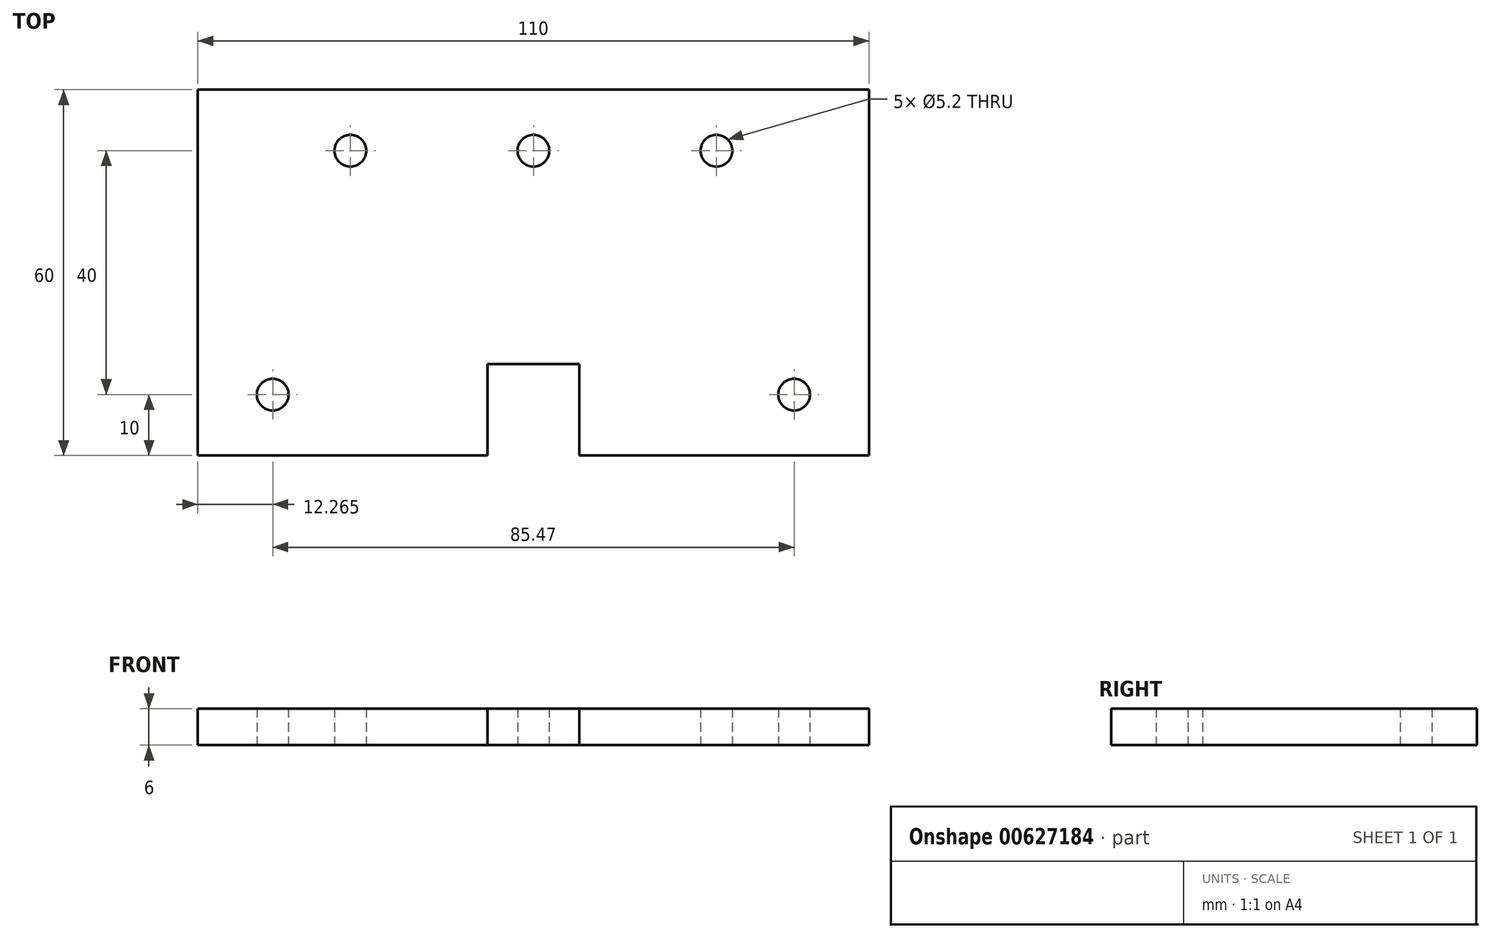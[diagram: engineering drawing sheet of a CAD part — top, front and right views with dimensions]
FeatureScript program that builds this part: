
annotation { "Feature Type Name" : "Feature", "Feature Type Description" : "" }
export const myFeature = defineFeature(function(context is Context, id is Id, definition is map)
    precondition{}
    {
        {
            var Q0;
            Q0=qCreatedBy(makeId("Top.planeOp"),FACE);
            var sketch = newSketch(context, id + "F0", { "sketchPlane" : qUnion([Q0])});
            skLineSegment(sketch, "E0.bottom", {"start": v(0, 0) * mm, "end": v(-110, 0) * mm});
            skLineSegment(sketch, "E0.top", {"start": v(0, 60) * mm, "end": v(-110, 60) * mm});
            skLineSegment(sketch, "E0.left", {"start": v(0, 0) * mm, "end": v(0, 60) * mm});
            skLineSegment(sketch, "E0.right", {"start": v(-110, 0) * mm, "end": v(-110, 60) * mm});
            skLineSegment(sketch, "E1", {"start": v(-110, 50) * mm, "end": v(0, 50) * mm, "construction": true});
            skCircle(sketch, "E2", {"center": v(-85, 50) * mm, "radius": 2.6 * mm});
            skCircle(sketch, "E3.1.0.0", {"center": v(-55, 50) * mm, "radius": 2.6 * mm});
            skCircle(sketch, "E3.2.0.0", {"center": v(-25, 50) * mm, "radius": 2.6 * mm});
            skLineSegment(sketch, "E3.direction1", {"start": v(-85, 50) * mm, "end": v(-55, 50) * mm, "construction": true});
            skLineSegment(sketch, "E4", {"start": v(-110, 10) * mm, "end": v(0, 10) * mm, "construction": true});
            skCircle(sketch, "E5", {"center": v(-97.73, 10) * mm, "radius": 2.6 * mm});
            skCircle(sketch, "E6.1.0.0", {"center": v(-12.26, 10) * mm, "radius": 2.6 * mm});
            skLineSegment(sketch, "E6.direction1", {"start": v(-97.73, 10) * mm, "end": v(-12.26, 10) * mm, "construction": true});
            skLineSegment(sketch, "E7", {"start": v(-47.5, 0) * mm, "end": v(-47.5, 15) * mm});
            skLineSegment(sketch, "E8", {"start": v(-47.5, 15) * mm, "end": v(-62.5, 15) * mm});
            skLineSegment(sketch, "E9", {"start": v(-62.5, 15) * mm, "end": v(-62.5, 0) * mm});
            skSolve(sketch);
        }
        {
            var Q0;
            Q0=makeQuery(id+"F0.imprint","IMPRINT",FACE,{"disambiguationData":[TD([[makeQuery(id+"F0.imprint","IMPRINT",EDGE,{"derivedFrom":sQuery(id+"F0.wireOp",EDGE,"E0.top")}),1.0]])]});
            extrude(context, id + "F1", {"entities" : qUnion([Q0]), "depth" : 6 * mm, "offsetDistance" : 25 * mm});
        }
    });
